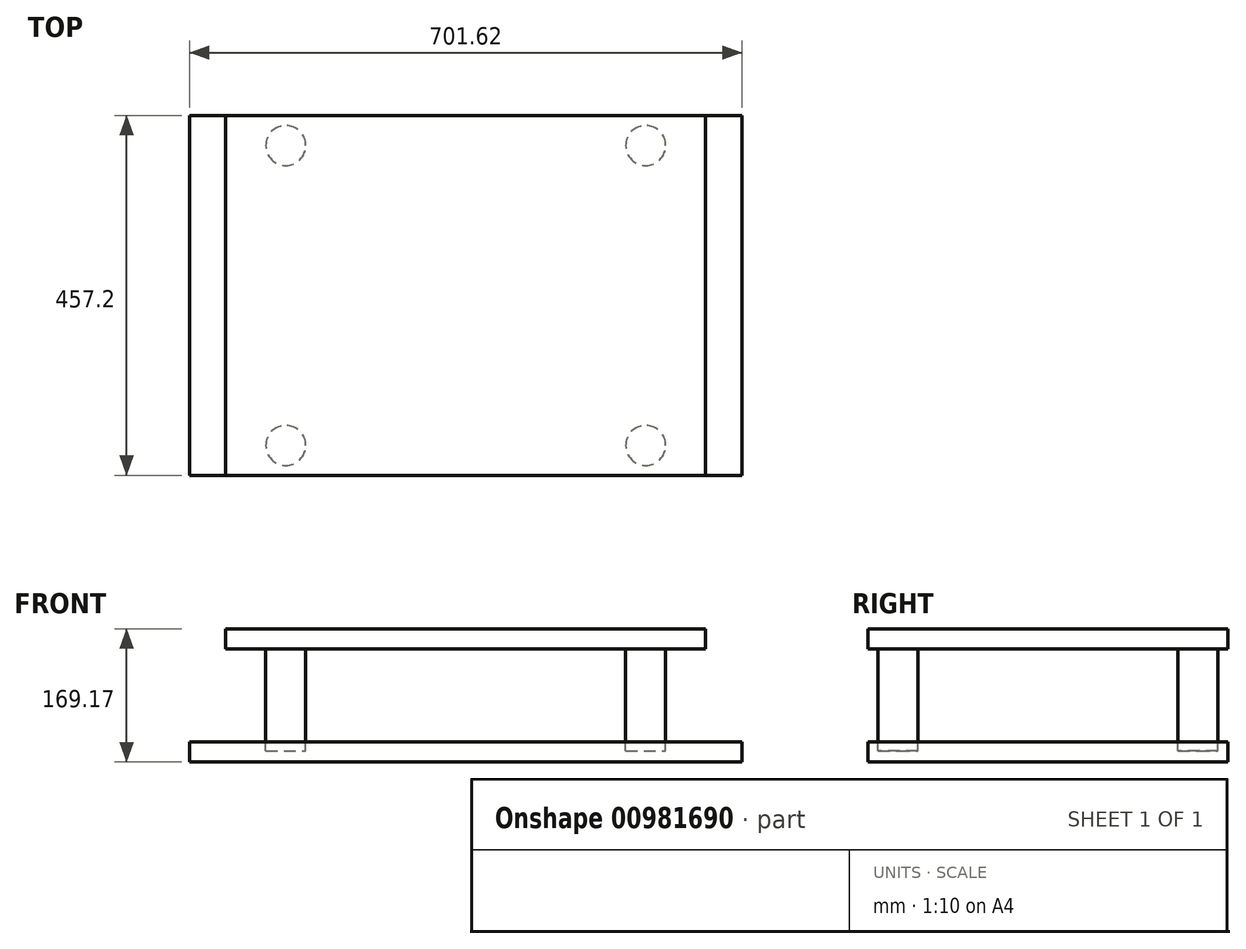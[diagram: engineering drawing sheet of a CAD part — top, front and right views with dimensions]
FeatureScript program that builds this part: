
annotation { "Feature Type Name" : "Feature", "Feature Type Description" : "" }
export const myFeature = defineFeature(function(context is Context, id is Id, definition is map)
    precondition{}
    {
        {
            var Q0;
            Q0=qCreatedBy(makeId("Front.planeOp"),FACE);
            var sketch = newSketch(context, id + "F0", { "sketchPlane" : qUnion([Q0])});
            skLineSegment(sketch, "E0.bottom", {"start": v(304.8, 95.84) * mm, "end": v(-304.8, 95.84) * mm});
            skLineSegment(sketch, "E0.top", {"start": v(304.8, 121.24) * mm, "end": v(-304.8, 121.24) * mm});
            skLineSegment(sketch, "E0.left", {"start": v(304.8, 95.84) * mm, "end": v(304.8, 121.24) * mm});
            skLineSegment(sketch, "E0.right", {"start": v(-304.8, 95.84) * mm, "end": v(-304.8, 121.24) * mm});
            skPoint(sketch, "E0.middle", {"position": v(0, 108.54) * mm});
            skLineSegment(sketch, "E1.bottom", {"start": v(350.81, -47.93) * mm, "end": v(-350.81, -47.93) * mm});
            skLineSegment(sketch, "E1.top", {"start": v(350.81, -22.53) * mm, "end": v(-350.81, -22.53) * mm});
            skLineSegment(sketch, "E1.left", {"start": v(350.81, -47.93) * mm, "end": v(350.81, -22.53) * mm});
            skLineSegment(sketch, "E1.right", {"start": v(-350.81, -47.93) * mm, "end": v(-350.81, -22.53) * mm});
            skPoint(sketch, "E1.middle", {"position": v(0, -35.23) * mm});
            skLineSegment(sketch, "E2", {"start": v(-304.8, 95.84) * mm, "end": v(-350.81, -22.53) * mm});
            skSolve(sketch);
        }
        {
            var Q0;
            Q0=makeQuery(id+"F0.imprint","IMPRINT",FACE,{"disambiguationData":[TD([[makeQuery(id+"F0.imprint","IMPRINT",EDGE,{"derivedFrom":sQuery(id+"F0.wireOp",EDGE,"E0.bottom")}),-1.0]])]});
            var Q1;
            Q1=makeQuery(id+"F0.imprint","IMPRINT",FACE,{"disambiguationData":[TD([[makeQuery(id+"F0.imprint","IMPRINT",EDGE,{"derivedFrom":sQuery(id+"F0.wireOp",EDGE,"E1.bottom")}),-1.0]])]});
            extrude(context, id + "F1", {"entities" : qUnion([Q0, Q1]), "depth" : 457.2 * mm, "offsetDistance" : 25.4 * mm});
        }
        {
            var Q0;
            Q0=makeQuery(id+"F1.opExtrude","SWEPT_FACE",FACE,{"disambiguationData":[OSD([sQuery(id+"F0.wireOp",EDGE,"E0.bottom")])]});
            var sketch = newSketch(context, id + "F2", { "sketchPlane" : qUnion([Q0])});
            skLineSegment(sketch, "E3", {"start": v(304.8, 457.2) * mm, "end": v(304.8, 419.1) * mm});
            skLineSegment(sketch, "E4", {"start": v(304.8, 0) * mm, "end": v(304.8, 38.1) * mm});
            skLineSegment(sketch, "E5", {"start": v(-304.8, 457.2) * mm, "end": v(-304.8, 419.1) * mm});
            skLineSegment(sketch, "E6", {"start": v(-304.8, 0) * mm, "end": v(-304.8, 38.1) * mm});
            skLineSegment(sketch, "E7", {"start": v(-304.8, 419.1) * mm, "end": v(-228.6, 419.1) * mm});
            skLineSegment(sketch, "E8", {"start": v(-304.8, 38.1) * mm, "end": v(-228.6, 38.1) * mm});
            skLineSegment(sketch, "E9", {"start": v(304.8, 38.1) * mm, "end": v(228.6, 38.1) * mm});
            skLineSegment(sketch, "E10", {"start": v(304.8, 419.1) * mm, "end": v(228.6, 419.1) * mm});
            skCircle(sketch, "E11", {"center": v(-228.6, 419.1) * mm, "radius": 25.4 * mm});
            skCircle(sketch, "E12", {"center": v(228.6, 419.1) * mm, "radius": 25.4 * mm});
            skCircle(sketch, "E13", {"center": v(228.6, 38.1) * mm, "radius": 25.4 * mm});
            skCircle(sketch, "E14", {"center": v(-228.6, 38.1) * mm, "radius": 25.4 * mm});
            skSolve(sketch);
        }
        {
            var Q0;
            Q0=qSketchRegion(id+"F2",true);
            extrude(context, id + "F3", {"entities" : qUnion([Q0]), "depth" : 129.54 * mm, "offsetDistance" : 25.4 * mm});
        }
    });
